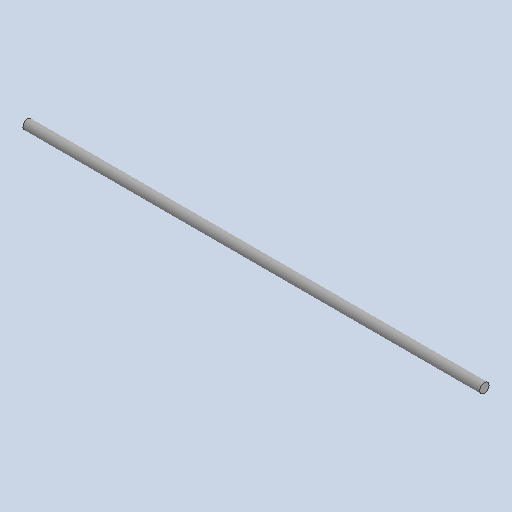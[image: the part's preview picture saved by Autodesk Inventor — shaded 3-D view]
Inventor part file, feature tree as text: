
AUTODESK INVENTOR PART (.ipt)
format: ipt  version: 2025.1 (Build 291241020, 241B)  size: 240,128 bytes
history: native  units: in
note: dims shown in document units (in); Inventor stores cm internally (conversion verified against a paired STEP export)
features: extrude x1, sketch x1
ambient origin geometry x8: Origin, YZ Plane, XZ Plane, XY Plane, X Axis, Y Axis, Z Axis, Center Point
bodies: Solid1 (feature_tree)
feature tree (2):
  extrude  "Extrusion1"  Depth=12.0in TaperAngle=0.0deg
  sketch  "Sketch1"  dims[d0=0.25in d1=12.0in d2=0.0in]
